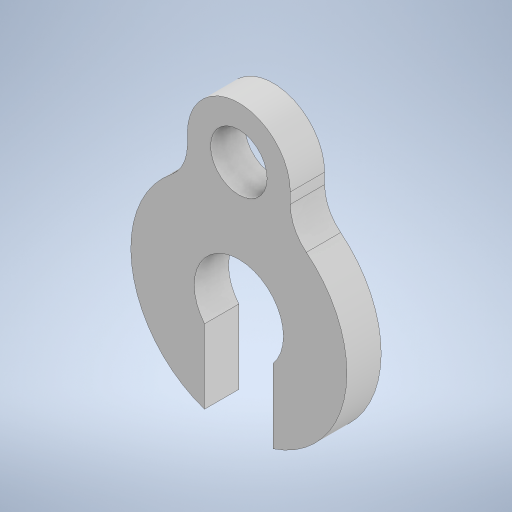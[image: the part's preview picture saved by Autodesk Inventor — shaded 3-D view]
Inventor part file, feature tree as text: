
AUTODESK INVENTOR PART (.ipt)
format: ipt  version: 2024 (Build 280153000, 153)  size: 266,240 bytes
history: native  units: in
note: dims shown in document units (in); Inventor stores cm internally (conversion verified against a paired STEP export)
features: extrude x1, fillet x1, direct_edit x1, sketch x1, other x1
ambient origin geometry x8: Origin, YZ Plane, XZ Plane, XY Plane, X Axis, Y Axis, Z Axis, Center Point
bodies: Solid1 (feature_tree)
feature tree (5):
  extrude  "Extrusion1"  Depth=0.3937in
  fillet  "Fillet1"  Radius=0.0825in
  direct_edit  "Direct Edit1"
  sketch  "Sketch1"  dims[d0=0.315in d1=0.13in d2=0.0825in d3=0.1in d4=0.1875in d5=0.15in d7=0.075in d8=0.15in d9=0.049in d10=0.1575in d11=0.1575in d12=0.049in d13=0.05in d14=0.0in d15=0.0625in d16=3.937in d17=0.3937in d18=0.3937in]
  other  "Scale1"
